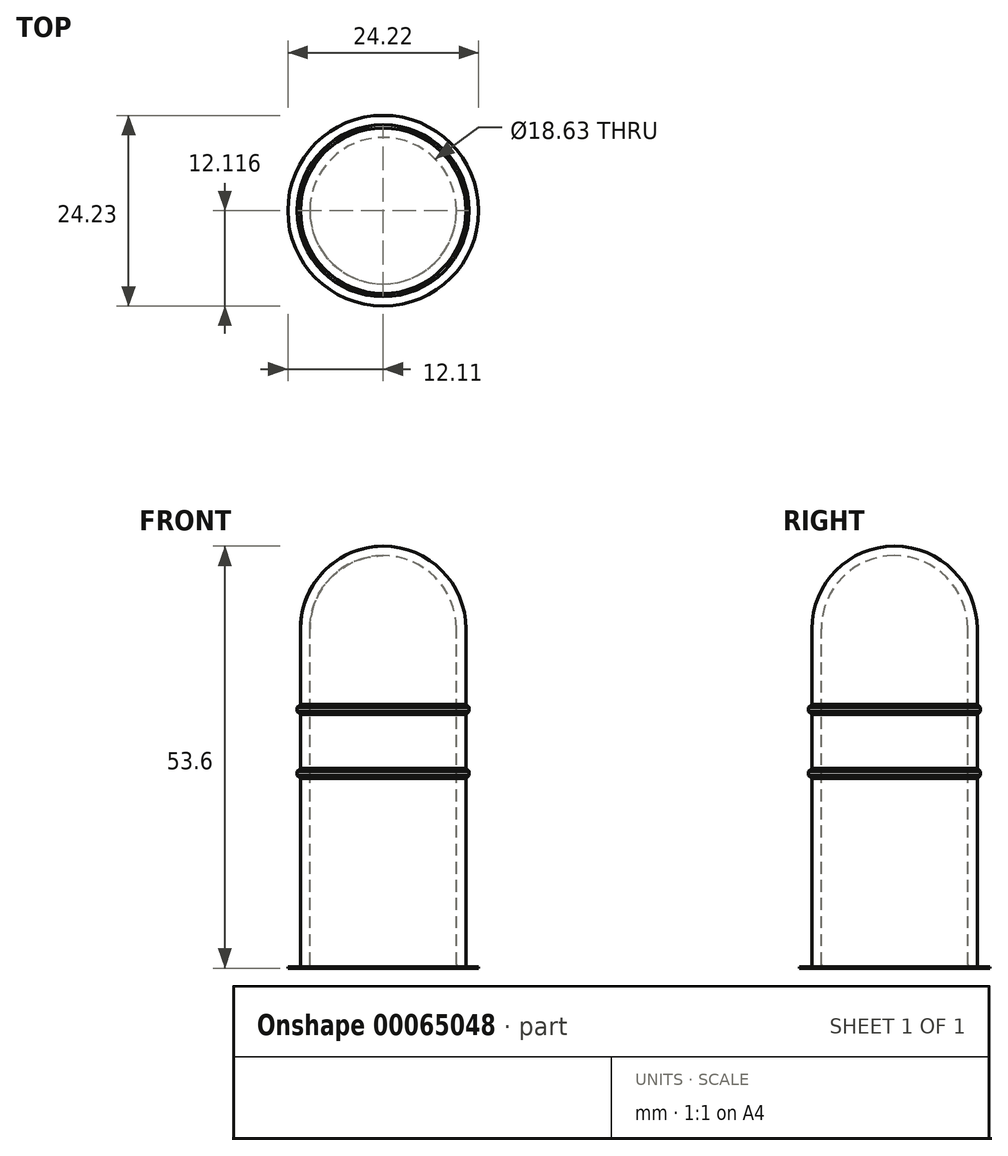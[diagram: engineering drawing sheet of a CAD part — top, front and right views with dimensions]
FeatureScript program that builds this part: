
annotation { "Feature Type Name" : "Feature", "Feature Type Description" : "" }
export const myFeature = defineFeature(function(context is Context, id is Id, definition is map)
    precondition{}
    {
        {
            var Q0;
            Q0=qCreatedBy(makeId("Front.planeOp"),FACE);
            var sketch = newSketch(context, id + "F0", { "sketchPlane" : qUnion([Q0])});
            skLineSegment(sketch, "E0", {"start": v(-9.31, 0) * mm, "end": v(-9.31, 43.08) * mm});
            skArc(sketch, "E1", {"start": v(-9.31, 43.08) * mm, "mid": v(-6.59, 49.67) * mm, "end": v(0, 52.4) * mm});
            skLineSegment(sketch, "E2", {"start": v(-10.51, 0) * mm, "end": v(-10.51, 43.08) * mm});
            skArc(sketch, "E3", {"start": v(-10.51, 43.08) * mm, "mid": v(-7.43, 50.52) * mm, "end": v(0, 53.6) * mm});
            skLineSegment(sketch, "E4", {"start": v(0, 53.6) * mm, "end": v(0, 52.4) * mm});
            skLineSegment(sketch, "E5", {"start": v(-10.51, 0) * mm, "end": v(-9.31, 0) * mm});
            skLineSegment(sketch, "E6", {"start": v(0, 52.4) * mm, "end": v(0, 0) * mm, "construction": true});
            skLineSegment(sketch, "E7.bottom", {"start": v(-10.51, 33.12) * mm, "end": v(-10.91, 33.12) * mm, "construction": true});
            skLineSegment(sketch, "E7.top", {"start": v(-10.51, 32.62) * mm, "end": v(-10.91, 32.62) * mm, "construction": true});
            skLineSegment(sketch, "E7.left", {"start": v(-10.51, 33.12) * mm, "end": v(-10.51, 32.62) * mm});
            skLineSegment(sketch, "E7.right", {"start": v(-10.91, 33.12) * mm, "end": v(-10.91, 32.62) * mm});
            skLineSegment(sketch, "E8.bottom", {"start": v(-10.51, 25) * mm, "end": v(-10.91, 25) * mm, "construction": true});
            skLineSegment(sketch, "E8.top", {"start": v(-10.51, 24.5) * mm, "end": v(-10.91, 24.5) * mm, "construction": true});
            skLineSegment(sketch, "E8.left", {"start": v(-10.51, 25) * mm, "end": v(-10.51, 24.5) * mm});
            skLineSegment(sketch, "E8.right", {"start": v(-10.91, 25) * mm, "end": v(-10.91, 24.5) * mm});
            skLineSegment(sketch, "E9", {"start": v(-10.91, 33.12) * mm, "end": v(-10.51, 33.52) * mm});
            skLineSegment(sketch, "E10", {"start": v(-10.91, 32.62) * mm, "end": v(-10.51, 32.22) * mm});
            skLineSegment(sketch, "E11", {"start": v(-10.91, 25) * mm, "end": v(-10.51, 25.4) * mm});
            skLineSegment(sketch, "E12", {"start": v(-10.91, 24.5) * mm, "end": v(-10.51, 24.1) * mm});
            skSolve(sketch);
        }
        {
            var Q0;
            {Q0=qUnion([makeQuery(id+"F0.imprint","IMPRINT",FACE,{"disambiguationData":[TD([[makeQuery(id+"F0.imprint","IMPRINT",EDGE,{"derivedFrom":sQuery(id+"F0.wireOp",EDGE,"E7.right")}),1.0]])]}),makeQuery(id+"F0.imprint","IMPRINT",FACE,{"disambiguationData":[TD([[makeQuery(id+"F0.imprint","IMPRINT",EDGE,{"derivedFrom":sQuery(id+"F0.wireOp",EDGE,"E8.right")}),1.0]])]}),makeQuery(id+"F0.imprint","IMPRINT",FACE,{"disambiguationData":[TD([[makeQuery(id+"F0.imprint","IMPRINT",EDGE,{"derivedFrom":sQuery(id+"F0.wireOp",EDGE,"E0")}),1.0]])]})]);}
            var Q1;
            Q1=sQuery(id+"F0.wireOp",EDGE,"E6");
            revolve(context, id + "F1", {"entities" : qUnion([Q0]), "axis" : qUnion([Q1]), "revolveType" : RevolveType.FULL});
        }
        {
            var Q0;
            Q0=makeQuery(id+"F1.opRevolve","SWEPT_EDGE",EDGE,{"disambiguationData":[OSD([sQuery(id+"F0.wireOp",EDGE,"E0"),sQuery(id+"F0.wireOp",EDGE,"E5")])]});
            fillet(context, id + "F2", {"entities" : qUnion([Q0]), "radius" : 0.5 * mm, "allowEdgeOverflow" : false});
        }
        {
            var Q0;
            Q0=qCreatedBy(makeId("Top.planeOp"),FACE);
            var sketch = newSketch(context, id + "F3", { "sketchPlane" : qUnion([Q0])});
            skCircle(sketch, "E13.0", {"center": v(0, 0) * mm, "radius": 10.51 * mm});
            skCircle(sketch, "E14.0", {"center": v(0, 0) * mm, "radius": 12.11 * mm});
            skLineSegment(sketch, "E15", {"start": v(0, 0) * mm, "end": v(0, 13.72) * mm, "construction": true});
            skSolve(sketch);
        }
        {
            var Q0;
            Q0=qSketchRegion(id+"F3",true);
            extrude(context, id + "F4", {"entities" : qUnion([Q0]), "operationType" : NewBodyOperationType.ADD, "depth" : 0.15 * mm});
        }
        {
            var Q0;
            Q0=makeQuery(id+"F1.opRevolve","SWEPT_BODY",BODY,{"disambiguationData":[OSD([sQuery(id+"F0.wireOp",EDGE,"E0"),sQuery(id+"F0.wireOp",EDGE,"E1"),sQuery(id+"F0.wireOp",EDGE,"E2"),sQuery(id+"F0.wireOp",EDGE,"E3"),sQuery(id+"F0.wireOp",EDGE,"E4"),sQuery(id+"F0.wireOp",EDGE,"E5"),sQuery(id+"F0.wireOp",EDGE,"E7.right"),sQuery(id+"F0.wireOp",EDGE,"E8.right"),sQuery(id+"F0.wireOp",EDGE,"E9"),sQuery(id+"F0.wireOp",EDGE,"E10"),sQuery(id+"F0.wireOp",EDGE,"E11"),sQuery(id+"F0.wireOp",EDGE,"E12")])]});
            var Q1;
            Q1=sQuery(id+"F3.wireOp",EDGE,"E15");
            transform(context, id + "F5", {"entities" : qUnion([Q0]), "transformType" : TransformType.TRANSLATION_ENTITY, "oppositeDirectionEntity" : false, "transformLine" : qUnion([Q1]), "makeCopy" : false});
        }
    });
